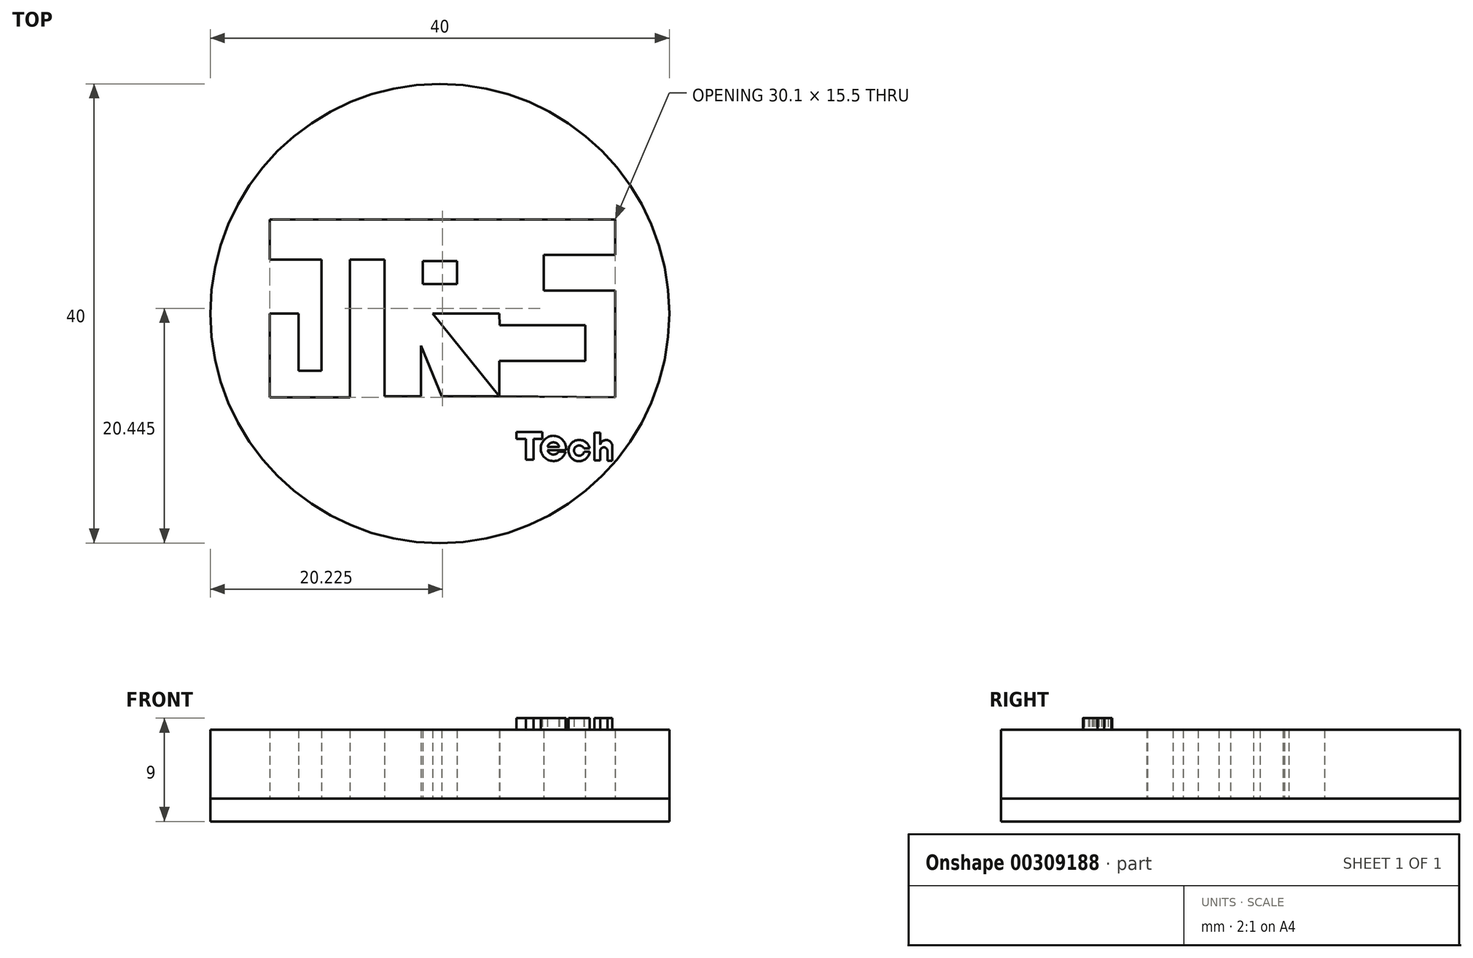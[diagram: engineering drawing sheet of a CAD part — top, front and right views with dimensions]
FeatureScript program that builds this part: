
annotation { "Feature Type Name" : "Feature", "Feature Type Description" : "" }
export const myFeature = defineFeature(function(context is Context, id is Id, definition is map)
    precondition{}
    {
        {
            var Q0;
            Q0=qCreatedBy(makeId("Top.planeOp"),FACE);
            var sketch = newSketch(context, id + "F0", { "sketchPlane" : qUnion([Q0])});
            skLineSegment(sketch, "E0", {"start": v(-14.82, 8.2) * mm, "end": v(-4.82, 8.2) * mm});
            skLineSegment(sketch, "E1", {"start": v(-4.82, 4.7) * mm, "end": v(-7.82, 4.7) * mm});
            skLineSegment(sketch, "E2", {"start": v(-7.82, 4.7) * mm, "end": v(-7.82, -7.3) * mm});
            skLineSegment(sketch, "E3", {"start": v(-7.82, -7.3) * mm, "end": v(-14.82, -7.3) * mm});
            skLineSegment(sketch, "E4", {"start": v(-14.82, -7.3) * mm, "end": v(-14.82, 0) * mm});
            skLineSegment(sketch, "E5", {"start": v(-14.82, 0) * mm, "end": v(-12.32, 0) * mm});
            skLineSegment(sketch, "E6", {"start": v(-12.32, 0) * mm, "end": v(-12.32, -5) * mm});
            skLineSegment(sketch, "E7", {"start": v(-12.32, -5) * mm, "end": v(-10.32, -5) * mm});
            skLineSegment(sketch, "E8", {"start": v(-10.32, -5) * mm, "end": v(-10.32, 4.7) * mm});
            skLineSegment(sketch, "E9", {"start": v(-10.32, 4.7) * mm, "end": v(-14.82, 4.7) * mm});
            skLineSegment(sketch, "E10", {"start": v(-14.82, 4.7) * mm, "end": v(-14.82, 8.2) * mm});
            skLineSegment(sketch, "E11", {"start": v(-4.82, 4.7) * mm, "end": v(-4.82, -7.22) * mm});
            skLineSegment(sketch, "E12", {"start": v(-4.82, 8.2) * mm, "end": v(5.18, 8.2) * mm});
            skLineSegment(sketch, "E13", {"start": v(5.18, 8.2) * mm, "end": v(5.18, 0) * mm});
            skLineSegment(sketch, "E14", {"start": v(5.18, 0) * mm, "end": v(-0.62, 0) * mm});
            skLineSegment(sketch, "E15", {"start": v(-0.62, 0) * mm, "end": v(5.18, -7.22) * mm});
            skLineSegment(sketch, "E16", {"start": v(5.18, -7.22) * mm, "end": v(0.18, -7.22) * mm});
            skLineSegment(sketch, "E17", {"start": v(0.18, -7.22) * mm, "end": v(-1.63, -2.81) * mm});
            skLineSegment(sketch, "E18", {"start": v(-1.63, -2.81) * mm, "end": v(-1.63, -7.22) * mm});
            skLineSegment(sketch, "E19", {"start": v(-1.63, -7.22) * mm, "end": v(-4.82, -7.22) * mm});
            skLineSegment(sketch, "E20", {"start": v(-1.5, 4.57) * mm, "end": v(-1.5, 2.57) * mm});
            skLineSegment(sketch, "E21", {"start": v(-1.5, 2.57) * mm, "end": v(1.5, 2.57) * mm});
            skLineSegment(sketch, "E22", {"start": v(1.5, 2.57) * mm, "end": v(1.5, 4.57) * mm});
            skLineSegment(sketch, "E23", {"start": v(1.5, 4.57) * mm, "end": v(-1.5, 4.57) * mm});
            skLineSegment(sketch, "E24", {"start": v(5.18, 8.2) * mm, "end": v(15.27, 8.2) * mm});
            skLineSegment(sketch, "E25", {"start": v(15.27, 8.2) * mm, "end": v(15.27, 5.1) * mm});
            skLineSegment(sketch, "E26", {"start": v(15.27, 5.1) * mm, "end": v(9.05, 5.1) * mm});
            skLineSegment(sketch, "E27", {"start": v(9.05, 5.1) * mm, "end": v(9.05, 2) * mm});
            skLineSegment(sketch, "E28", {"start": v(9.05, 2) * mm, "end": v(15.27, 2) * mm});
            skLineSegment(sketch, "E29", {"start": v(15.27, 2) * mm, "end": v(15.27, -7.3) * mm});
            skLineSegment(sketch, "E30", {"start": v(15.27, -7.3) * mm, "end": v(5.18, -7.22) * mm});
            skLineSegment(sketch, "E31", {"start": v(12.67, -1.02) * mm, "end": v(12.67, -4.12) * mm});
            skLineSegment(sketch, "E32", {"start": v(12.67, -4.12) * mm, "end": v(5.18, -4.12) * mm});
            skLineSegment(sketch, "E33", {"start": v(5.18, -4.12) * mm, "end": v(5.18, -7.22) * mm});
            skLineSegment(sketch, "E34", {"start": v(12.67, -1.02) * mm, "end": v(5.22, -1.02) * mm});
            skLineSegment(sketch, "E35", {"start": v(5.22, -1.02) * mm, "end": v(5.18, 0) * mm});
            skCircle(sketch, "E36", {"center": v(0, 0) * mm, "radius": 20 * mm});
            skPoint(sketch, "E36.centerSnap0", {"position": v(0, 2.57) * mm});
            skLineSegment(sketch, "E37", {"start": v(-4.82, 8.2) * mm, "end": v(-4.82, 4.7) * mm});
            skSolve(sketch);
        }
        {
            var Q0;
            Q0=makeQuery(id+"F0.imprint","IMPRINT",FACE,{"disambiguationData":[TD([[makeQuery(id+"F0.imprint","IMPRINT",EDGE,{"derivedFrom":sQuery(id+"F0.wireOp",EDGE,"E0")}),1.0]])]});
            extrude(context, id + "F1", {"entities" : qUnion([Q0]), "depth" : 6 * mm});
        }
        {
            var Q0;
            Q0=makeQuery(id+"F0.imprint","IMPRINT",FACE,{"disambiguationData":[TD([[makeQuery(id+"F0.imprint","IMPRINT",EDGE,{"derivedFrom":sQuery(id+"F0.wireOp",EDGE,"E20")}),1.0]])]});
            extrude(context, id + "F2", {"entities" : qUnion([Q0]), "depth" : 6 * mm});
        }
        {
            var Q0;
            Q0=makeQuery(id+"F0.imprint","IMPRINT",FACE,{"disambiguationData":[TD([[makeQuery(id+"F0.imprint","IMPRINT",EDGE,{"derivedFrom":sQuery(id+"F0.wireOp",EDGE,"E14")}),1.0]])]});
            extrude(context, id + "F3", {"entities" : qUnion([Q0]), "depth" : 6 * mm});
        }
        {
            var Q0;
            Q0=sQuery(id+"F0.wireOp",EDGE,"UN9D2Q1s-by0P-w3r3-fo7E-CWs4w5GKjAeQ");
            var Q1;
            Q1=sQuery(id+"F0.wireOp",EDGE,"E13");
            extrude(context, id + "F4", {"bodyType" : ToolBodyType.SURFACE, "surfaceEntities" : qUnion([Q0, Q1]), "depth" : 6 * mm});
        }
        {
            var Q0;
            Q0=sQuery(id+"F0.wireOp",EDGE,"E37");
            extrude(context, id + "F5", {"bodyType" : ToolBodyType.SURFACE, "surfaceEntities" : qUnion([Q0]), "depth" : 6 * mm});
        }
        {
            var Q0;
            Q0=makeQuery(id+"F0.imprint","IMPRINT",FACE,{"disambiguationData":[TD([[makeQuery(id+"F0.imprint","IMPRINT",EDGE,{"derivedFrom":sQuery(id+"F0.wireOp",EDGE,"E0")}),-1.0]])]});
            var sketch = newSketch(context, id + "F6", { "sketchPlane" : qUnion([Q0])});
            skCircle(sketch, "E38", {"center": v(0, 0) * mm, "radius": 20 * mm});
            skSolve(sketch);
        }
        {
            var Q0;
            Q0 = qSketchRegion(id + "F6", true);
            extrude(context, id + "F7", {"entities" : qUnion([Q0]), "depth" : -2 * mm});
        }
        {
            var Q0;
            Q0=makeQuery(id+"F1.opExtrude","CAP_FACE",FACE,{"disambiguationData":[OSD([sQuery(id+"F0.wireOp",EDGE,"E0"),sQuery(id+"F0.wireOp",EDGE,"E1"),sQuery(id+"F0.wireOp",EDGE,"E2"),sQuery(id+"F0.wireOp",EDGE,"E3"),sQuery(id+"F0.wireOp",EDGE,"E4"),sQuery(id+"F0.wireOp",EDGE,"E5"),sQuery(id+"F0.wireOp",EDGE,"E6"),sQuery(id+"F0.wireOp",EDGE,"E7"),sQuery(id+"F0.wireOp",EDGE,"E8"),sQuery(id+"F0.wireOp",EDGE,"E9"),sQuery(id+"F0.wireOp",EDGE,"E10"),sQuery(id+"F0.wireOp",EDGE,"E11"),sQuery(id+"F0.wireOp",EDGE,"E12"),sQuery(id+"F0.wireOp",EDGE,"E16"),sQuery(id+"F0.wireOp",EDGE,"E17"),sQuery(id+"F0.wireOp",EDGE,"E18"),sQuery(id+"F0.wireOp",EDGE,"E19"),sQuery(id+"F0.wireOp",EDGE,"E24"),sQuery(id+"F0.wireOp",EDGE,"E25"),sQuery(id+"F0.wireOp",EDGE,"E26"),sQuery(id+"F0.wireOp",EDGE,"E27"),sQuery(id+"F0.wireOp",EDGE,"E28"),sQuery(id+"F0.wireOp",EDGE,"E29"),sQuery(id+"F0.wireOp",EDGE,"E30"),sQuery(id+"F0.wireOp",EDGE,"E36")])],"isStart":false});
            var sketch = newSketch(context, id + "F8", { "sketchPlane" : qUnion([Q0])});
            skLineSegment(sketch, "E39", {"start": v(6.68, -10.33) * mm, "end": v(6.68, -10.93) * mm});
            skLineSegment(sketch, "E40", {"start": v(6.68, -10.93) * mm, "end": v(7.5, -10.93) * mm});
            skLineSegment(sketch, "E41", {"start": v(7.5, -10.93) * mm, "end": v(7.5, -12.73) * mm});
            skLineSegment(sketch, "E42", {"start": v(7.5, -12.73) * mm, "end": v(8.17, -12.73) * mm});
            skLineSegment(sketch, "E43", {"start": v(8.17, -12.73) * mm, "end": v(8.17, -10.93) * mm});
            skLineSegment(sketch, "E44", {"start": v(8.17, -10.93) * mm, "end": v(8.92, -10.93) * mm});
            skLineSegment(sketch, "E45", {"start": v(8.92, -10.93) * mm, "end": v(8.92, -10.33) * mm});
            skLineSegment(sketch, "E46", {"start": v(8.92, -10.33) * mm, "end": v(6.68, -10.33) * mm});
            skCircle(sketch, "E47", {"center": v(9.9, -11.75) * mm, "radius": 1.1 * mm});
            skCircle(sketch, "E48", {"center": v(9.9, -11.75) * mm, "radius": 0.53 * mm});
            skLineSegment(sketch, "E49", {"start": v(10.4, -11.91) * mm, "end": v(10.98, -11.91) * mm});
            skLineSegment(sketch, "E50", {"start": v(10.41, -11.62) * mm, "end": v(9.38, -11.62) * mm});
            skLineSegment(sketch, "E51", {"start": v(10.4, -11.91) * mm, "end": v(9.38, -11.91) * mm});
            skLineSegment(sketch, "E52", {"start": v(10.35, -12.03) * mm, "end": v(10.96, -12.03) * mm});
            skCircle(sketch, "E53", {"center": v(12.14, -11.94) * mm, "radius": 0.93 * mm});
            skCircle(sketch, "E54", {"center": v(12.14, -11.94) * mm, "radius": 0.45 * mm});
            skLineSegment(sketch, "E55", {"start": v(12.54, -11.74) * mm, "end": v(13.04, -11.74) * mm});
            skLineSegment(sketch, "E56", {"start": v(12.57, -12.05) * mm, "end": v(13.06, -12.05) * mm});
            skLineSegment(sketch, "E57", {"start": v(10.41, -11.62) * mm, "end": v(10.99, -11.62) * mm});
            skLineSegment(sketch, "E58", {"start": v(13.47, -10.37) * mm, "end": v(13.47, -12.81) * mm});
            skLineSegment(sketch, "E59", {"start": v(13.47, -12.81) * mm, "end": v(13.98, -12.81) * mm});
            skLineSegment(sketch, "E60", {"start": v(13.98, -12.81) * mm, "end": v(13.98, -11.97) * mm});
            skLineSegment(sketch, "E61", {"start": v(13.47, -10.37) * mm, "end": v(13.97, -10.37) * mm});
            skLineSegment(sketch, "E62", {"start": v(13.97, -10.37) * mm, "end": v(13.97, -11.55) * mm});
            skCircle(sketch, "E63", {"center": v(14.3, -11.97) * mm, "radius": 0.32 * mm});
            skLineSegment(sketch, "E64", {"start": v(14.6, -12.82) * mm, "end": v(15.03, -12.82) * mm});
            skCircle(sketch, "E65", {"center": v(14.5, -11.56) * mm, "radius": 0.54 * mm});
            skLineSegment(sketch, "E66", {"start": v(14.6, -11.99) * mm, "end": v(14.6, -12.08) * mm});
            skLineSegment(sketch, "E67", {"start": v(14.6, -12.08) * mm, "end": v(14.6, -12.82) * mm});
            skLineSegment(sketch, "E68", {"start": v(15.03, -12.82) * mm, "end": v(15.03, -11.58) * mm});
            skSolve(sketch);
        }
        {
            var Q0;
            Q0=makeQuery(id+"F8.imprint","IMPRINT",FACE,{"disambiguationData":[TD([[makeQuery(id+"F8.imprint","IMPRINT",EDGE,{"derivedFrom":sQuery(id+"F8.wireOp",EDGE,"E64")}),1.0]])]});
            var Q1;
            {var subQ5=sQuery(id+"F8.wireOp",EDGE,"E66");Q1=makeQuery(id+"F8.imprint","IMPRINT",FACE,{"disambiguationData":[TD([[makeQuery(id+"F8.imprint","IMPRINT",EDGE,{"derivedFrom":subQ5}),1.0]])]});}
            var Q2;
            Q2=makeQuery(id+"F8.imprint","IMPRINT",FACE,{"disambiguationData":[TD([[makeQuery(id+"F8.imprint","IMPRINT",EDGE,{"derivedFrom":sQuery(id+"F8.wireOp",EDGE,"E58")}),1.0]])]});
            var Q3;
            {var subQ0=sQuery(id+"F8.wireOp",EDGE,"E55");Q3=makeQuery(id+"F8.imprint","IMPRINT",FACE,{"disambiguationData":[TD([[makeQuery(id+"F8.imprint","IMPRINT",EDGE,{"derivedFrom":subQ0}),1.0]])]});}
            var Q4;
            {var subQ5=sQuery(id+"F8.wireOp",EDGE,"E52");Q4=makeQuery(id+"F8.imprint","IMPRINT",FACE,{"disambiguationData":[TD([[makeQuery(id+"F8.imprint","IMPRINT",EDGE,{"derivedFrom":subQ5}),-1.0]])]});}
            var Q5;
            {var subQ0=sQuery(id+"F8.wireOp",EDGE,"E49");Q5=makeQuery(id+"F8.imprint","IMPRINT",FACE,{"disambiguationData":[TD([[makeQuery(id+"F8.imprint","IMPRINT",EDGE,{"derivedFrom":subQ0}),1.0]])]});}
            var Q6;
            {var subQ0=sQuery(id+"F8.wireOp",EDGE,"E50");Q6=makeQuery(id+"F8.imprint","IMPRINT",FACE,{"disambiguationData":[TD([[makeQuery(id+"F8.imprint","IMPRINT",EDGE,{"derivedFrom":subQ0}),1.0]])]});}
            var Q7;
            Q7=makeQuery(id+"F8.imprint","IMPRINT",FACE,{"disambiguationData":[TD([[makeQuery(id+"F8.imprint","IMPRINT",EDGE,{"derivedFrom":sQuery(id+"F8.wireOp",EDGE,"E39")}),1.0]])]});
            extrude(context, id + "F9", {"entities" : qUnion([Q0, Q1, Q2, Q3, Q4, Q5, Q6, Q7]), "operationType" : NewBodyOperationType.ADD, "depth" : 1 * mm});
        }
    });
